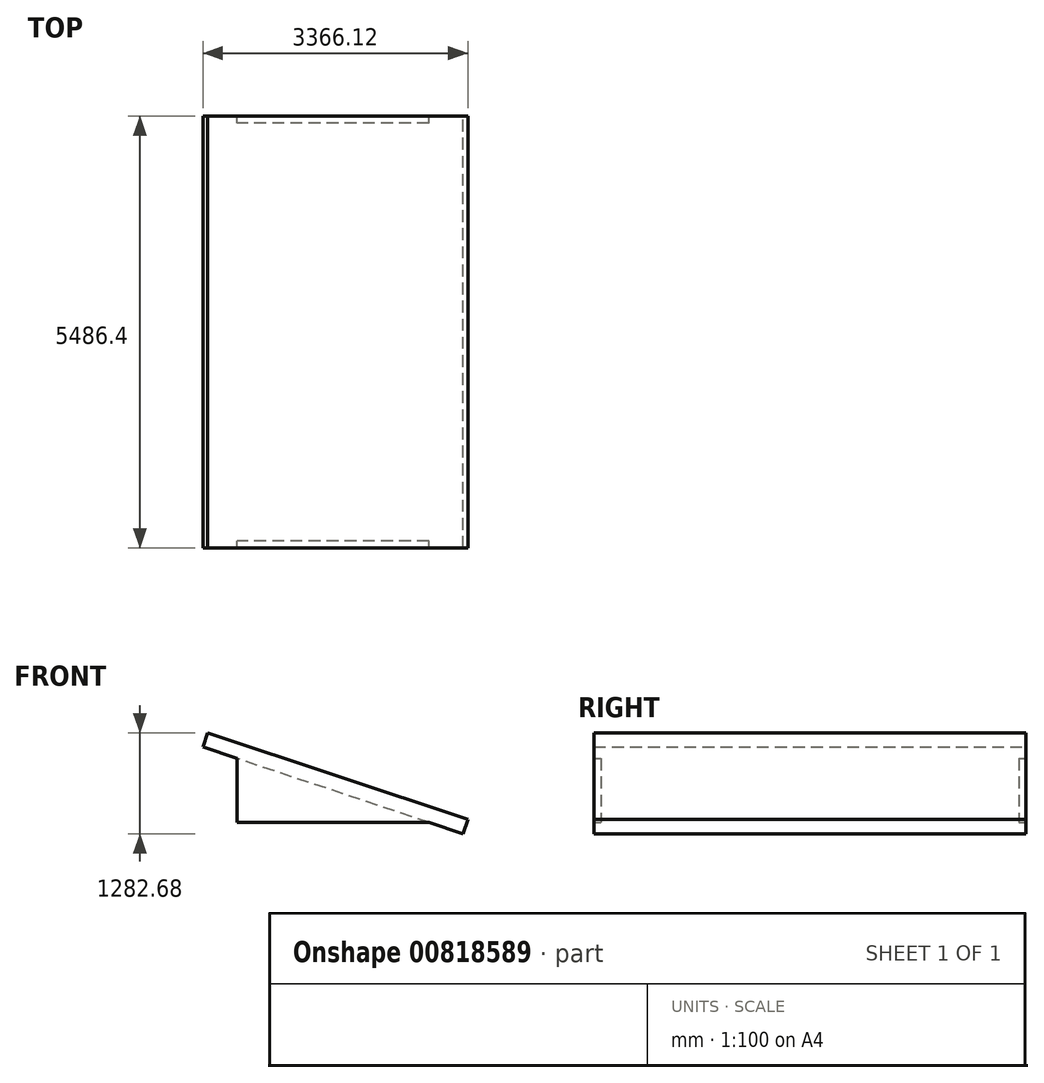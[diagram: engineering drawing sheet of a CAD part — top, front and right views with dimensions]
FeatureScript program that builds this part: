
annotation { "Feature Type Name" : "Feature", "Feature Type Description" : "" }
export const myFeature = defineFeature(function(context is Context, id is Id, definition is map)
    precondition{}
    {
        {
            var Q0;
            Q0=qCreatedBy(makeId("Front.planeOp"),FACE);
            var sketch = newSketch(context, id + "F0", { "sketchPlane" : qUnion([Q0])});
            skLineSegment(sketch, "E0.bottom", {"start": v(0, 0) * mm, "end": v(2438.4, 0) * mm});
            skLineSegment(sketch, "E0.left", {"start": v(0, 0) * mm, "end": v(0, 812.8) * mm});
            skLineSegment(sketch, "E1", {"start": v(-433.74, 957.38) * mm, "end": v(2872.14, -144.58) * mm});
            skLineSegment(sketch, "E2.0", {"start": v(-373.5, 1138.1) * mm, "end": v(2932.38, 36.14) * mm});
            skLineSegment(sketch, "E3", {"start": v(2438.4, 0) * mm, "end": v(2498.64, 180.72) * mm});
            skLineSegment(sketch, "E4", {"start": v(0, 812.8) * mm, "end": v(60.24, 993.52) * mm});
            skLineSegment(sketch, "E5.0", {"start": v(2872.14, -144.58) * mm, "end": v(2932.38, 36.14) * mm});
            skLineSegment(sketch, "E6.0", {"start": v(-433.74, 957.38) * mm, "end": v(-373.5, 1138.1) * mm});
            skSolve(sketch);
        }
        {
            var Q0;
            {var subQ0=sQuery(id+"F0.wireOp",EDGE,"E4");Q0=makeQuery(id+"F0.imprint","IMPRINT",FACE,{"disambiguationData":[TD([[makeQuery(id+"F0.imprint","IMPRINT",EDGE,{"derivedFrom":subQ0}),1.0]])]});}
            var Q1;
            {var subQ0=sQuery(id+"F0.wireOp",EDGE,"E3");Q1=makeQuery(id+"F0.imprint","IMPRINT",FACE,{"disambiguationData":[TD([[makeQuery(id+"F0.imprint","IMPRINT",EDGE,{"derivedFrom":subQ0}),1.0]])]});}
            var Q2;
            {var subQ0=sQuery(id+"F0.wireOp",EDGE,"E3");Q2=makeQuery(id+"F0.imprint","IMPRINT",FACE,{"disambiguationData":[TD([[makeQuery(id+"F0.imprint","IMPRINT",EDGE,{"derivedFrom":subQ0}),-1.0]])]});}
            var Q3;
            {var subQ0=sQuery(id+"F0.wireOp",EDGE,"E0.bottom");Q3=makeQuery(id+"F0.imprint","IMPRINT",FACE,{"disambiguationData":[TD([[makeQuery(id+"F0.imprint","IMPRINT",EDGE,{"derivedFrom":subQ0}),1.0]])]});}
            extrude(context, id + "F1", {"entities" : qUnion([Q0, Q1, Q2, Q3]), "depth" : 5486.4 * mm, "offsetDistance" : 25.4 * mm});
        }
        {
            var Q0;
            Q0=makeQuery(id+"F1.opExtrude","SWEPT_FACE",FACE,{"disambiguationData":[OSD([sQuery(id+"F0.wireOp",EDGE,"E6.0")])]});
            var sketch = newSketch(context, id + "F2", { "sketchPlane" : qUnion([Q0])});
            skLineSegment(sketch, "E7.bottom", {"start": v(88.9, 771.09) * mm, "end": v(5397.5, 771.09) * mm});
            skLineSegment(sketch, "E7.top", {"start": v(88.9, -41.71) * mm, "end": v(5397.5, -41.71) * mm});
            skLineSegment(sketch, "E7.left", {"start": v(88.9, 771.09) * mm, "end": v(88.9, -41.71) * mm});
            skLineSegment(sketch, "E7.right", {"start": v(5397.5, 771.09) * mm, "end": v(5397.5, -41.71) * mm});
            skSolve(sketch);
        }
        {
            var Q0;
            Q0 = qSketchRegion(id + "F2", true);
            extrude(context, id + "F3", {"entities" : qUnion([Q0]), "operationType" : NewBodyOperationType.REMOVE, "oppositeDirection" : true, "depth" : 3352.8 * mm, "offsetDistance" : 25.4 * mm});
        }
    });
